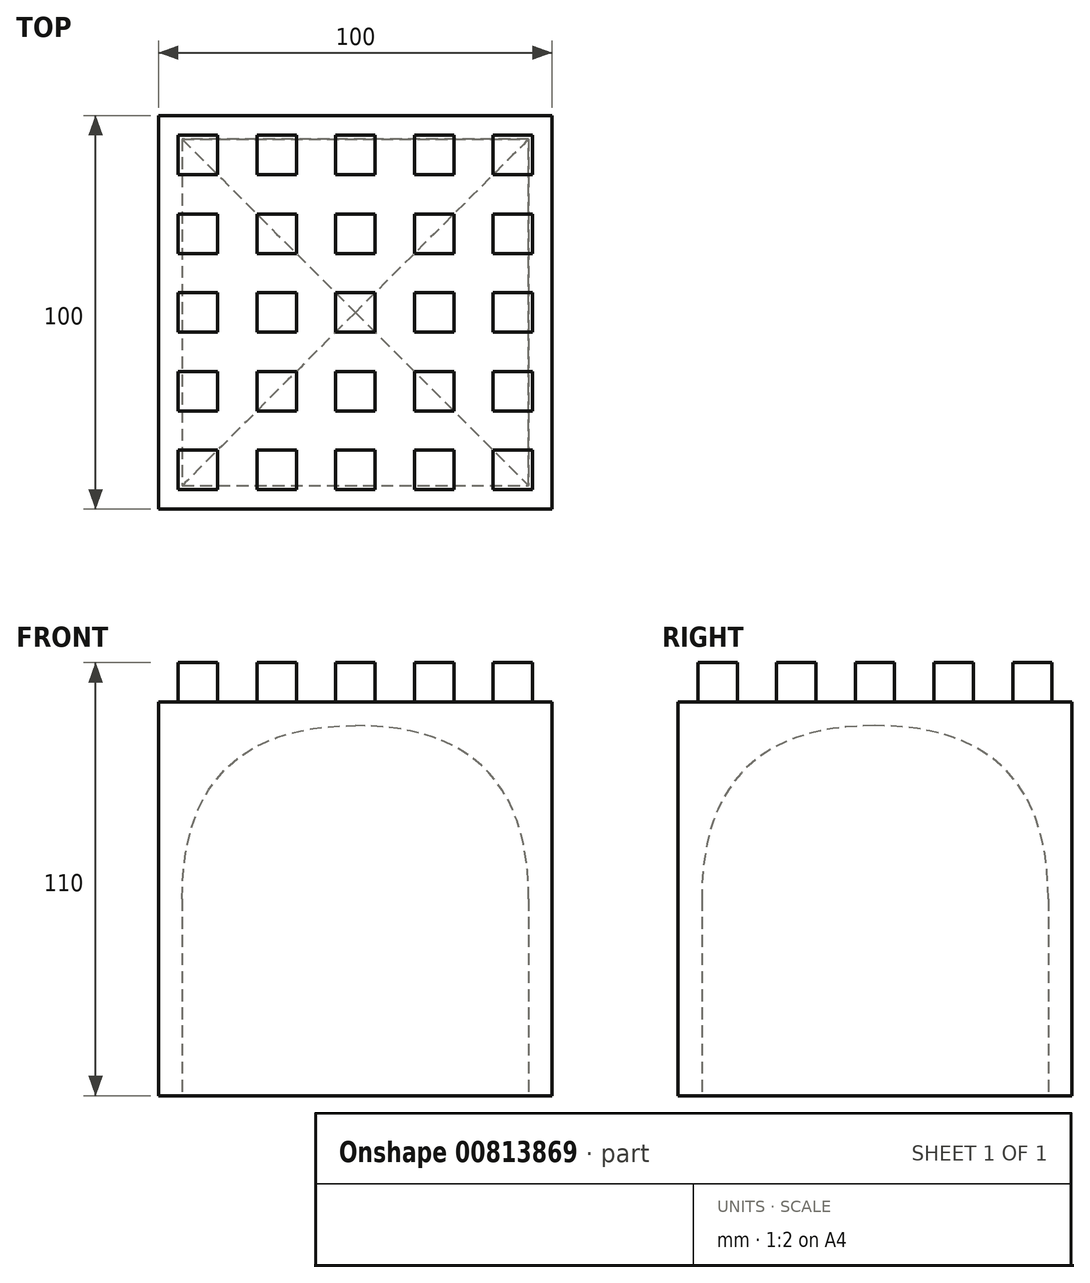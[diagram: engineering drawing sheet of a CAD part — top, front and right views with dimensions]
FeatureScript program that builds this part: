
annotation { "Feature Type Name" : "Feature", "Feature Type Description" : "" }
export const myFeature = defineFeature(function(context is Context, id is Id, definition is map)
    precondition{}
    {
        {
            var Q0;
            Q0=qCreatedBy(makeId("Top.planeOp"),FACE);
            var sketch = newSketch(context, id + "F0", { "sketchPlane" : qUnion([Q0])});
            skLineSegment(sketch, "E0.bottom", {"start": v(-50, 50) * mm, "end": v(50, 50) * mm});
            skLineSegment(sketch, "E0.top", {"start": v(-50, -50) * mm, "end": v(50, -50) * mm});
            skLineSegment(sketch, "E0.left", {"start": v(-50, 50) * mm, "end": v(-50, -50) * mm});
            skLineSegment(sketch, "E0.right", {"start": v(50, 50) * mm, "end": v(50, -50) * mm});
            skSolve(sketch);
        }
        {
            var Q0;
            Q0 = qSketchRegion(id + "F0", true);
            extrude(context, id + "F1", {"entities" : qUnion([Q0]), "depth" : 100 * mm, "offsetDistance" : 25 * mm});
        }
        {
            var Q0;
            Q0=makeQuery(id+"F1.opExtrude","CAP_FACE",FACE,{"disambiguationData":[OSD([sQuery(id+"F0.wireOp",EDGE,"E0.bottom"),sQuery(id+"F0.wireOp",EDGE,"E0.top"),sQuery(id+"F0.wireOp",EDGE,"E0.left"),sQuery(id+"F0.wireOp",EDGE,"E0.right")])],"isStart":false});
            var sketch = newSketch(context, id + "F2", { "sketchPlane" : qUnion([Q0])});
            skLineSegment(sketch, "E1.bottom", {"start": v(-45, -35) * mm, "end": v(-35, -35) * mm});
            skLineSegment(sketch, "E1.top", {"start": v(-45, -45) * mm, "end": v(-35, -45) * mm});
            skLineSegment(sketch, "E1.left", {"start": v(-45, -35) * mm, "end": v(-45, -45) * mm});
            skLineSegment(sketch, "E1.right", {"start": v(-35, -35) * mm, "end": v(-35, -45) * mm});
            skLineSegment(sketch, "E2.0.1.0", {"start": v(-35, -15) * mm, "end": v(-35, -25) * mm});
            skLineSegment(sketch, "E2.0.1.1", {"start": v(-45, -15) * mm, "end": v(-45, -25) * mm});
            skLineSegment(sketch, "E2.0.1.2", {"start": v(-45, -15) * mm, "end": v(-35, -15) * mm});
            skLineSegment(sketch, "E2.0.1.3", {"start": v(-45, -25) * mm, "end": v(-35, -25) * mm});
            skLineSegment(sketch, "E2.0.2.0", {"start": v(-35, 5) * mm, "end": v(-35, -5) * mm});
            skLineSegment(sketch, "E2.0.2.1", {"start": v(-45, 5) * mm, "end": v(-45, -5) * mm});
            skLineSegment(sketch, "E2.0.2.2", {"start": v(-45, 5) * mm, "end": v(-35, 5) * mm});
            skLineSegment(sketch, "E2.0.2.3", {"start": v(-45, -5) * mm, "end": v(-35, -5) * mm});
            skLineSegment(sketch, "E2.0.3.0", {"start": v(-35, 25) * mm, "end": v(-35, 15) * mm});
            skLineSegment(sketch, "E2.0.3.1", {"start": v(-45, 25) * mm, "end": v(-45, 15) * mm});
            skLineSegment(sketch, "E2.0.3.2", {"start": v(-45, 25) * mm, "end": v(-35, 25) * mm});
            skLineSegment(sketch, "E2.0.3.3", {"start": v(-45, 15) * mm, "end": v(-35, 15) * mm});
            skLineSegment(sketch, "E2.0.4.0", {"start": v(-35, 45) * mm, "end": v(-35, 35) * mm});
            skLineSegment(sketch, "E2.0.4.1", {"start": v(-45, 45) * mm, "end": v(-45, 35) * mm});
            skLineSegment(sketch, "E2.0.4.2", {"start": v(-45, 45) * mm, "end": v(-35, 45) * mm});
            skLineSegment(sketch, "E2.0.4.3", {"start": v(-45, 35) * mm, "end": v(-35, 35) * mm});
            skLineSegment(sketch, "E2.1.0.0", {"start": v(-15, -35) * mm, "end": v(-15, -45) * mm});
            skLineSegment(sketch, "E2.1.0.1", {"start": v(-25, -35) * mm, "end": v(-25, -45) * mm});
            skLineSegment(sketch, "E2.1.0.2", {"start": v(-25, -35) * mm, "end": v(-15, -35) * mm});
            skLineSegment(sketch, "E2.1.0.3", {"start": v(-25, -45) * mm, "end": v(-15, -45) * mm});
            skLineSegment(sketch, "E2.1.1.0", {"start": v(-15, -15) * mm, "end": v(-15, -25) * mm});
            skLineSegment(sketch, "E2.1.1.1", {"start": v(-25, -15) * mm, "end": v(-25, -25) * mm});
            skLineSegment(sketch, "E2.1.1.2", {"start": v(-25, -15) * mm, "end": v(-15, -15) * mm});
            skLineSegment(sketch, "E2.1.1.3", {"start": v(-25, -25) * mm, "end": v(-15, -25) * mm});
            skLineSegment(sketch, "E2.1.2.0", {"start": v(-15, 5) * mm, "end": v(-15, -5) * mm});
            skLineSegment(sketch, "E2.1.2.1", {"start": v(-25, 5) * mm, "end": v(-25, -5) * mm});
            skLineSegment(sketch, "E2.1.2.2", {"start": v(-25, 5) * mm, "end": v(-15, 5) * mm});
            skLineSegment(sketch, "E2.1.2.3", {"start": v(-25, -5) * mm, "end": v(-15, -5) * mm});
            skLineSegment(sketch, "E2.1.3.0", {"start": v(-15, 25) * mm, "end": v(-15, 15) * mm});
            skLineSegment(sketch, "E2.1.3.1", {"start": v(-25, 25) * mm, "end": v(-25, 15) * mm});
            skLineSegment(sketch, "E2.1.3.2", {"start": v(-25, 25) * mm, "end": v(-15, 25) * mm});
            skLineSegment(sketch, "E2.1.3.3", {"start": v(-25, 15) * mm, "end": v(-15, 15) * mm});
            skLineSegment(sketch, "E2.1.4.0", {"start": v(-15, 45) * mm, "end": v(-15, 35) * mm});
            skLineSegment(sketch, "E2.1.4.1", {"start": v(-25, 45) * mm, "end": v(-25, 35) * mm});
            skLineSegment(sketch, "E2.1.4.2", {"start": v(-25, 45) * mm, "end": v(-15, 45) * mm});
            skLineSegment(sketch, "E2.1.4.3", {"start": v(-25, 35) * mm, "end": v(-15, 35) * mm});
            skLineSegment(sketch, "E2.2.0.0", {"start": v(5, -35) * mm, "end": v(5, -45) * mm});
            skLineSegment(sketch, "E2.2.0.1", {"start": v(-5, -35) * mm, "end": v(-5, -45) * mm});
            skLineSegment(sketch, "E2.2.0.2", {"start": v(-5, -35) * mm, "end": v(5, -35) * mm});
            skLineSegment(sketch, "E2.2.0.3", {"start": v(-5, -45) * mm, "end": v(5, -45) * mm});
            skLineSegment(sketch, "E2.2.1.0", {"start": v(5, -15) * mm, "end": v(5, -25) * mm});
            skLineSegment(sketch, "E2.2.1.1", {"start": v(-5, -15) * mm, "end": v(-5, -25) * mm});
            skLineSegment(sketch, "E2.2.1.2", {"start": v(-5, -15) * mm, "end": v(5, -15) * mm});
            skLineSegment(sketch, "E2.2.1.3", {"start": v(-5, -25) * mm, "end": v(5, -25) * mm});
            skLineSegment(sketch, "E2.2.2.0", {"start": v(5, 5) * mm, "end": v(5, -5) * mm});
            skLineSegment(sketch, "E2.2.2.1", {"start": v(-5, 5) * mm, "end": v(-5, -5) * mm});
            skLineSegment(sketch, "E2.2.2.2", {"start": v(-5, 5) * mm, "end": v(5, 5) * mm});
            skLineSegment(sketch, "E2.2.2.3", {"start": v(-5, -5) * mm, "end": v(5, -5) * mm});
            skLineSegment(sketch, "E2.2.3.0", {"start": v(5, 25) * mm, "end": v(5, 15) * mm});
            skLineSegment(sketch, "E2.2.3.1", {"start": v(-5, 25) * mm, "end": v(-5, 15) * mm});
            skLineSegment(sketch, "E2.2.3.2", {"start": v(-5, 25) * mm, "end": v(5, 25) * mm});
            skLineSegment(sketch, "E2.2.3.3", {"start": v(-5, 15) * mm, "end": v(5, 15) * mm});
            skLineSegment(sketch, "E2.2.4.0", {"start": v(5, 45) * mm, "end": v(5, 35) * mm});
            skLineSegment(sketch, "E2.2.4.1", {"start": v(-5, 45) * mm, "end": v(-5, 35) * mm});
            skLineSegment(sketch, "E2.2.4.2", {"start": v(-5, 45) * mm, "end": v(5, 45) * mm});
            skLineSegment(sketch, "E2.2.4.3", {"start": v(-5, 35) * mm, "end": v(5, 35) * mm});
            skLineSegment(sketch, "E2.3.0.0", {"start": v(25, -35) * mm, "end": v(25, -45) * mm});
            skLineSegment(sketch, "E2.3.0.1", {"start": v(15, -35) * mm, "end": v(15, -45) * mm});
            skLineSegment(sketch, "E2.3.0.2", {"start": v(15, -35) * mm, "end": v(25, -35) * mm});
            skLineSegment(sketch, "E2.3.0.3", {"start": v(15, -45) * mm, "end": v(25, -45) * mm});
            skLineSegment(sketch, "E2.3.1.0", {"start": v(25, -15) * mm, "end": v(25, -25) * mm});
            skLineSegment(sketch, "E2.3.1.1", {"start": v(15, -15) * mm, "end": v(15, -25) * mm});
            skLineSegment(sketch, "E2.3.1.2", {"start": v(15, -15) * mm, "end": v(25, -15) * mm});
            skLineSegment(sketch, "E2.3.1.3", {"start": v(15, -25) * mm, "end": v(25, -25) * mm});
            skLineSegment(sketch, "E2.3.2.0", {"start": v(25, 5) * mm, "end": v(25, -5) * mm});
            skLineSegment(sketch, "E2.3.2.1", {"start": v(15, 5) * mm, "end": v(15, -5) * mm});
            skLineSegment(sketch, "E2.3.2.2", {"start": v(15, 5) * mm, "end": v(25, 5) * mm});
            skLineSegment(sketch, "E2.3.2.3", {"start": v(15, -5) * mm, "end": v(25, -5) * mm});
            skLineSegment(sketch, "E2.3.3.0", {"start": v(25, 25) * mm, "end": v(25, 15) * mm});
            skLineSegment(sketch, "E2.3.3.1", {"start": v(15, 25) * mm, "end": v(15, 15) * mm});
            skLineSegment(sketch, "E2.3.3.2", {"start": v(15, 25) * mm, "end": v(25, 25) * mm});
            skLineSegment(sketch, "E2.3.3.3", {"start": v(15, 15) * mm, "end": v(25, 15) * mm});
            skLineSegment(sketch, "E2.3.4.0", {"start": v(25, 45) * mm, "end": v(25, 35) * mm});
            skLineSegment(sketch, "E2.3.4.1", {"start": v(15, 45) * mm, "end": v(15, 35) * mm});
            skLineSegment(sketch, "E2.3.4.2", {"start": v(15, 45) * mm, "end": v(25, 45) * mm});
            skLineSegment(sketch, "E2.3.4.3", {"start": v(15, 35) * mm, "end": v(25, 35) * mm});
            skLineSegment(sketch, "E2.4.0.0", {"start": v(45, -35) * mm, "end": v(45, -45) * mm});
            skLineSegment(sketch, "E2.4.0.1", {"start": v(35, -35) * mm, "end": v(35, -45) * mm});
            skLineSegment(sketch, "E2.4.0.2", {"start": v(35, -35) * mm, "end": v(45, -35) * mm});
            skLineSegment(sketch, "E2.4.0.3", {"start": v(35, -45) * mm, "end": v(45, -45) * mm});
            skLineSegment(sketch, "E2.4.1.0", {"start": v(45, -15) * mm, "end": v(45, -25) * mm});
            skLineSegment(sketch, "E2.4.1.1", {"start": v(35, -15) * mm, "end": v(35, -25) * mm});
            skLineSegment(sketch, "E2.4.1.2", {"start": v(35, -15) * mm, "end": v(45, -15) * mm});
            skLineSegment(sketch, "E2.4.1.3", {"start": v(35, -25) * mm, "end": v(45, -25) * mm});
            skLineSegment(sketch, "E2.4.2.0", {"start": v(45, 5) * mm, "end": v(45, -5) * mm});
            skLineSegment(sketch, "E2.4.2.1", {"start": v(35, 5) * mm, "end": v(35, -5) * mm});
            skLineSegment(sketch, "E2.4.2.2", {"start": v(35, 5) * mm, "end": v(45, 5) * mm});
            skLineSegment(sketch, "E2.4.2.3", {"start": v(35, -5) * mm, "end": v(45, -5) * mm});
            skLineSegment(sketch, "E2.4.3.0", {"start": v(45, 25) * mm, "end": v(45, 15) * mm});
            skLineSegment(sketch, "E2.4.3.1", {"start": v(35, 25) * mm, "end": v(35, 15) * mm});
            skLineSegment(sketch, "E2.4.3.2", {"start": v(35, 25) * mm, "end": v(45, 25) * mm});
            skLineSegment(sketch, "E2.4.3.3", {"start": v(35, 15) * mm, "end": v(45, 15) * mm});
            skLineSegment(sketch, "E2.4.4.0", {"start": v(45, 45) * mm, "end": v(45, 35) * mm});
            skLineSegment(sketch, "E2.4.4.1", {"start": v(35, 45) * mm, "end": v(35, 35) * mm});
            skLineSegment(sketch, "E2.4.4.2", {"start": v(35, 45) * mm, "end": v(45, 45) * mm});
            skLineSegment(sketch, "E2.4.4.3", {"start": v(35, 35) * mm, "end": v(45, 35) * mm});
            skLineSegment(sketch, "E2.direction1", {"start": v(-40, -40) * mm, "end": v(-20, -40) * mm, "construction": true});
            skLineSegment(sketch, "E2.direction2", {"start": v(-40, -40) * mm, "end": v(-40, -20) * mm, "construction": true});
            skSolve(sketch);
        }
        {
            var Q0;
            Q0 = qSketchRegion(id + "F2", true);
            extrude(context, id + "F3", {"entities" : qUnion([Q0]), "operationType" : NewBodyOperationType.ADD, "depth" : 10 * mm, "offsetDistance" : 25 * mm});
        }
        {
            var Q0;
            Q0=makeQuery(id+"F1.opExtrude","CAP_FACE",FACE,{"disambiguationData":[OSD([sQuery(id+"F0.wireOp",EDGE,"E0.bottom"),sQuery(id+"F0.wireOp",EDGE,"E0.top"),sQuery(id+"F0.wireOp",EDGE,"E0.left"),sQuery(id+"F0.wireOp",EDGE,"E0.right")])],"isStart":true});
            shell(context, id + "F4", {"entities" : qUnion([Q0]), "thickness" : 6 * mm});
        }
        {
            var Q0;
            Q0=makeQuery(id+"F4.opShell","OFFSET_FACE",FACE,{"disambiguationData":[OSD([sQuery(id+"F0.wireOp",EDGE,"E0.bottom"),sQuery(id+"F0.wireOp",EDGE,"E0.top"),sQuery(id+"F0.wireOp",EDGE,"E0.left"),sQuery(id+"F0.wireOp",EDGE,"E0.right")])]});
            fillet(context, id + "F5", {"entities" : qUnion([Q0]), "radius" : 44 * mm, "tangentPropagation" : true, "rho" : 0.5, "crossSection" : FilletCrossSection.CONIC, "allowEdgeOverflow" : false});
        }
    });
